# Revit family: Showerhead-American_Standard-Townsend-1660515_Series
name_source: partatom
category: Plumbing Fixtures
units: mm (PartAtom-declared; Revit-internal decimal feet)

## family parameters
Always vertical = No
Cut with Voids When Loaded = No
OmniClass Number = 23.45.05.14.17
OmniClass Title = Showers
Part Type = Normal
Room Calculation Point = No
Round Connector Dimension = Use Diameter
Shared = Yes
Work Plane-Based = Yes

## types (5) — shared parameters
Assembly Code = D2010710
CEC Compliant = Yes
CW Connection = Yes
CWFU = 3
CalGreen Compliant = Yes
Compliance Certifications = These products meet or exceed: ASME A112.18.1, CSA B125.1
Default Elevation = 0"
Description = Town Square® S 6-1/4-Inch 1.8 gpm/6.8 L/min Fixed Showerhead
Flow Rate = 1.8 gpm(6.8 L/min)
HW Connection = Yes
HWFU = 3
Height = 2 11/16"
Length = 6 5/16"
Manufacturer = American Standard
Product Documentation Link = https://americanstandard.box.com
Product Page URL = https://www.americanstandard-us.com
URL = https://www.americanstandard-us.com
Vent Connection = No
WFU = 4
Waste Connection = No
Water Connection Diameter = 1/2"
Water Connection Radius = 1/4"
Width = 6 5/16"

## per-type parameters (varying)
| type | Finish | Material |
| 1660515.002 | Brass-American Standard-002-Polished Chrome | Brass-American Standard-002-Polished Chrome |
| 1660515.013 | Brass-American Standard-013-Polished Nickel | Brass-American Standard-013-Polished Nickel |
| 1660515.295 | Brass-American Standard-295-Satin Nickel | Brass-American Standard-295-Satin Nickel |
| 1660515.243 | Brass-American Standard-243-Matte Black | Brass-American Standard-243-Matte Black |
| 1660515.278 | Brass-American Standard-278-Legacy Bronze | Brass-American Standard-278-Legacy Bronze |

note: column(s) folded — value = type name in every type: Model

## geometry (parser evidence)
native form markers: Sweep x2
no freeform markers — native parametric forms only
